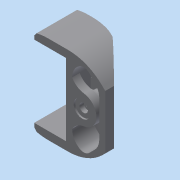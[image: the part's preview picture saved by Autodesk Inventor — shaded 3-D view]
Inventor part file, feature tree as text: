
AUTODESK INVENTOR PART (.ipt)
format: ipt  version: 2014 SP1 (Build 180222100, 222)  size: 446,464 bytes
history: native  units: in
note: dims shown in document units (in); Inventor stores cm internally (conversion verified against a paired STEP export)
features: extrude x12, chamfer x11, sketch x11, fillet x7, other x1, shell x1, projected_geometry x1
ambient origin geometry x8: Origin, YZ Plane, XZ Plane, XY Plane, X Axis, Y Axis, Z Axis, Center Point
bodies: Solid1 (feature_tree)
feature tree (44):
  other  "batterybox_sketch.ipt"
  extrude  "Extrusion1"  Depth=2.0in TaperAngle=0.0deg
  extrude  "Extrusion2"  Depth=0.201in
  extrude  "Extrusion4"  Depth=1.0in
  extrude  "Extrusion7"  Depth=0.375in
  extrude  "Extrusion8"  Depth=0.375in TaperAngle=0.0deg
  extrude  "Extrusion12"  Depth=0.1in TaperAngle=0.0deg
  extrude  "Extrusion13"  Depth=1.0in TaperAngle=0.0deg
  extrude  "Extrusion14"  Depth=0.5in
  chamfer  "Chamfer19"  Distance=1.0in
  fillet  "Fillet11"  Radius=1.5in
  extrude  "Extrusion15"  Depth=1.0in TaperAngle=45.0deg
  chamfer  "Chamfer20"  Distance=1.0in
  fillet  "Fillet16"  Radius=0.25in
  extrude  "Extrusion20"  Depth=0.375in TaperAngle=0.0deg
  chamfer  "Chamfer26"  Distance=0.375in Angle=45.0deg
  chamfer  "Chamfer27"  Distance=0.125in
  extrude  "Extrusion21"  Depth=0.95in
  chamfer  "Chamfer28"  Distance=1.5in
  chamfer  "Chamfer29"  Distance=1.45in Angle=45.0deg
  fillet  "Fillet19"  Radius=1.5625in
  extrude  "Extrusion22"  Depth=0.5in TaperAngle=0.0deg
  shell  "Shell1"  Thickness=0.5in
  fillet  "Fillet20"  Radius=0.5in
  chamfer  "Chamfer30"  Distance=58.5in
  chamfer  "Chamfer31"  Distance=0.5in
  chamfer  "Chamfer33"  [1 undecoded]
  fillet  "Fillet21"  Radius=0.5in
  fillet  "Fillet22"  Radius=0.375in
  fillet  "Fillet23"  Radius=1.0in
  chamfer  "Chamfer34"  Distance=0.05in Angle=45.0deg
  chamfer  "Chamfer36"  Distance=0.05in Angle=45.0deg
  sketch  "Sketch1"  dims[d0=0.3937in d1=2.0in d2=0.0in]
  sketch  "Sketch2"  dims[d3=2.0in d4=0.0in d22=0.201in]
  sketch  "Sketch7"  dims[d25=2.0in d26=1.0in]
  sketch  "Sketch8"  dims[d27=1.0in d28=0.0in d42=0.375in]
  sketch  "Sketch12"  dims[d43=0.05in d44=0.375in d45=0.0in]
  sketch  "Sketch13"  dims[d51=1.05in d52=0.1in d53=0.0in]
  sketch  "Sketch14"  dims[d110=1.3in d111=1.0in d112=0.0in]
  sketch  "Sketch15"  dims[d113=0.5in d114=0.5in]
  projected_geometry  "Projected Loop1"
  sketch  "Sketch20"  dims[d115=1.0in]
  sketch  "Sketch21"  dims[d116=1.0in]
  sketch  "Sketch22"  dims[d117=1.0in d118=1.0in d119=0.0in d120=1.5in d121=0.0in d122=1.0in d123=0.125in d124=45.0deg d125=1.0in d128=0.25in d129=0.375in d130=0.0in d131=0.375in d132=0.125in d133=45.0deg d157=0.125in d175=0.95in d176=1.5in d177=0.0in d178=1.45in d179=0.125in d180=45.0deg d181=1.5625in d182=0.125in d183=45.0deg d184=0.5in d185=0.0in d186=0.5in d187=0.125in d188=45.0deg d189=0.5in d190=0.125in d191=45.0deg d192=58.5in d193=0.5in d194=0.0in d195=0.5in d196=0.0in d197=0.375in d198=1.0in d199=0.05in d200=0.125in d201=45.0deg d202=0.05in d203=0.125in d204=45.0deg d208=0.125in d209=0.125in d210=45.0deg d211=3.0625in d212=0.5in d215=4.0in d217=0.5in d218=0.125in d219=45.0deg d223=0.15in d224=0.125in d225=45.0deg]
note: 1 required parameter value undecoded (feature->parameter linkage not recoverable at this tier; creation-order binding heuristic only, values carry confidence <= 0.55)
